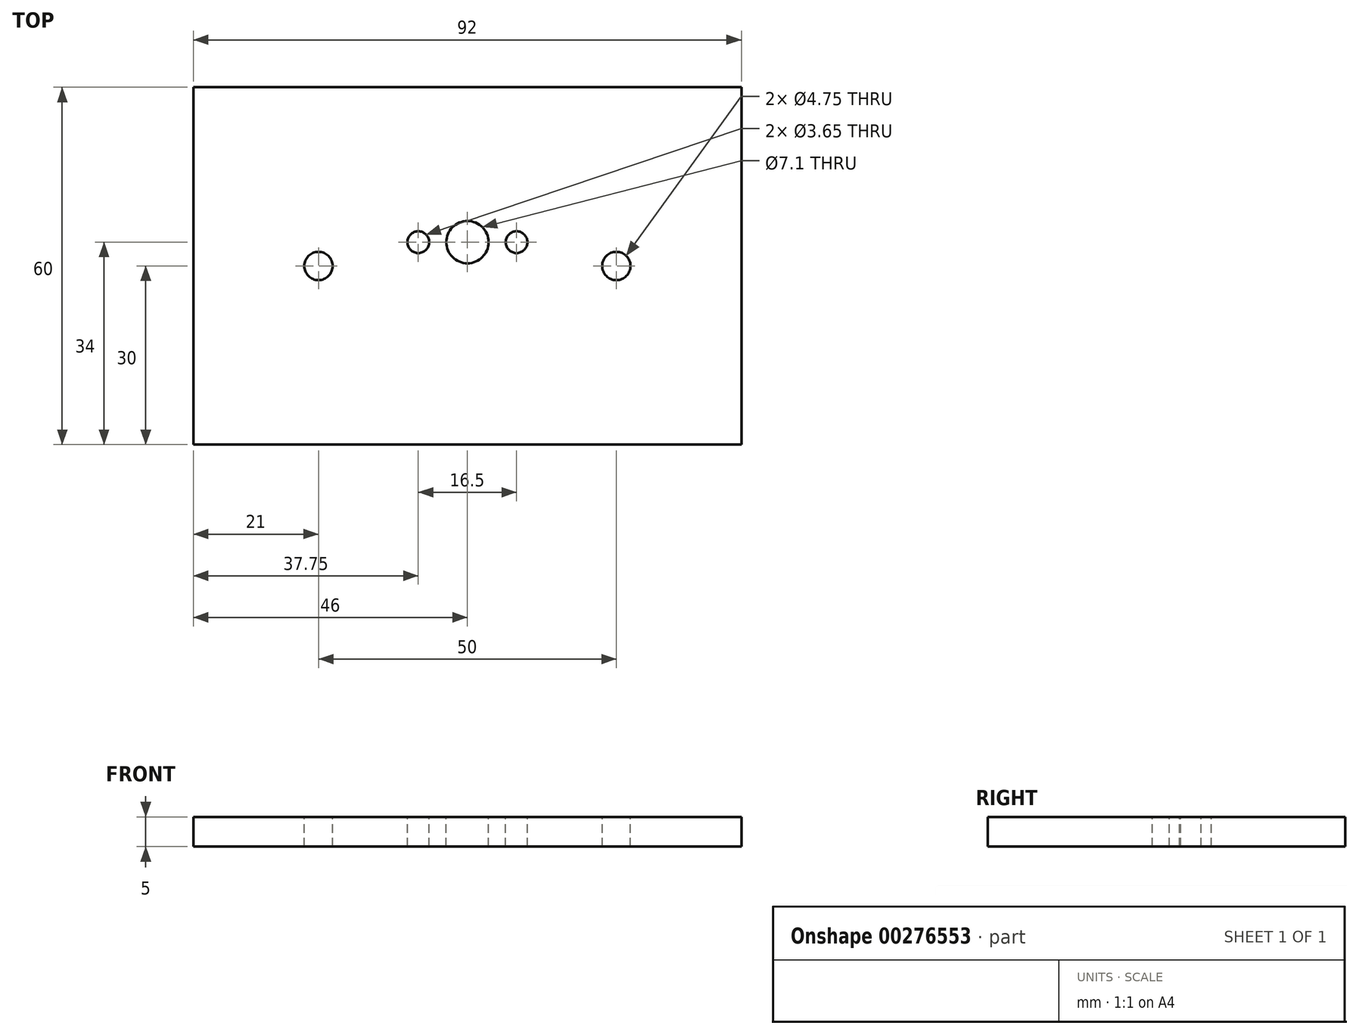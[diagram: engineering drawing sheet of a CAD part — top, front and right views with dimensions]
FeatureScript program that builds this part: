
annotation { "Feature Type Name" : "Feature", "Feature Type Description" : "" }
export const myFeature = defineFeature(function(context is Context, id is Id, definition is map)
    precondition{}
    {
        {
            var Q0;
            Q0=qCreatedBy(makeId("Top.planeOp"),FACE);
            var sketch = newSketch(context, id + "F0", { "sketchPlane" : qUnion([Q0])});
            skLineSegment(sketch, "E0.bottom", {"start": v(46, -30) * mm, "end": v(-46, -30) * mm});
            skLineSegment(sketch, "E0.top", {"start": v(46, 30) * mm, "end": v(-46, 30) * mm});
            skLineSegment(sketch, "E0.left", {"start": v(46, -30) * mm, "end": v(46, 30) * mm});
            skLineSegment(sketch, "E0.right", {"start": v(-46, -30) * mm, "end": v(-46, 30) * mm});
            skPoint(sketch, "E0.middle", {"position": v(0, 0) * mm});
            skSolve(sketch);
        }
        {
            var Q0;
            Q0 = qSketchRegion(id + "F0", true);
            extrude(context, id + "F1", {"entities" : qUnion([Q0]), "depth" : 5 * mm, "offsetDistance" : 25 * mm});
        }
        {
            var Q0;
            Q0=makeQuery(id+"F1.opExtrude","CAP_FACE",FACE,{"disambiguationData":[OSD([sQuery(id+"F0.wireOp",EDGE,"E0.bottom"),sQuery(id+"F0.wireOp",EDGE,"E0.top"),sQuery(id+"F0.wireOp",EDGE,"E0.left"),sQuery(id+"F0.wireOp",EDGE,"E0.right")])],"isStart":false});
            var sketch = newSketch(context, id + "F2", { "sketchPlane" : qUnion([Q0])});
            skPoint(sketch, "E1", {"position": v(0, 4) * mm});
            skCircle(sketch, "E2", {"center": v(0, 4) * mm, "radius": 3.55 * mm});
            skCircle(sketch, "E3", {"center": v(-8.25, 4) * mm, "radius": 1.82 * mm});
            skCircle(sketch, "E4", {"center": v(8.25, 4) * mm, "radius": 1.82 * mm});
            skCircle(sketch, "E5", {"center": v(-25, 0) * mm, "radius": 2.38 * mm});
            skCircle(sketch, "E6", {"center": v(25, 0) * mm, "radius": 2.38 * mm});
            skSolve(sketch);
        }
        {
            var Q0;
            Q0 = qSketchRegion(id + "F2", true);
            extrude(context, id + "F3", {"entities" : qUnion([Q0]), "operationType" : NewBodyOperationType.REMOVE, "oppositeDirection" : true, "depth" : 25 * mm, "offsetDistance" : 25 * mm});
        }
    });
